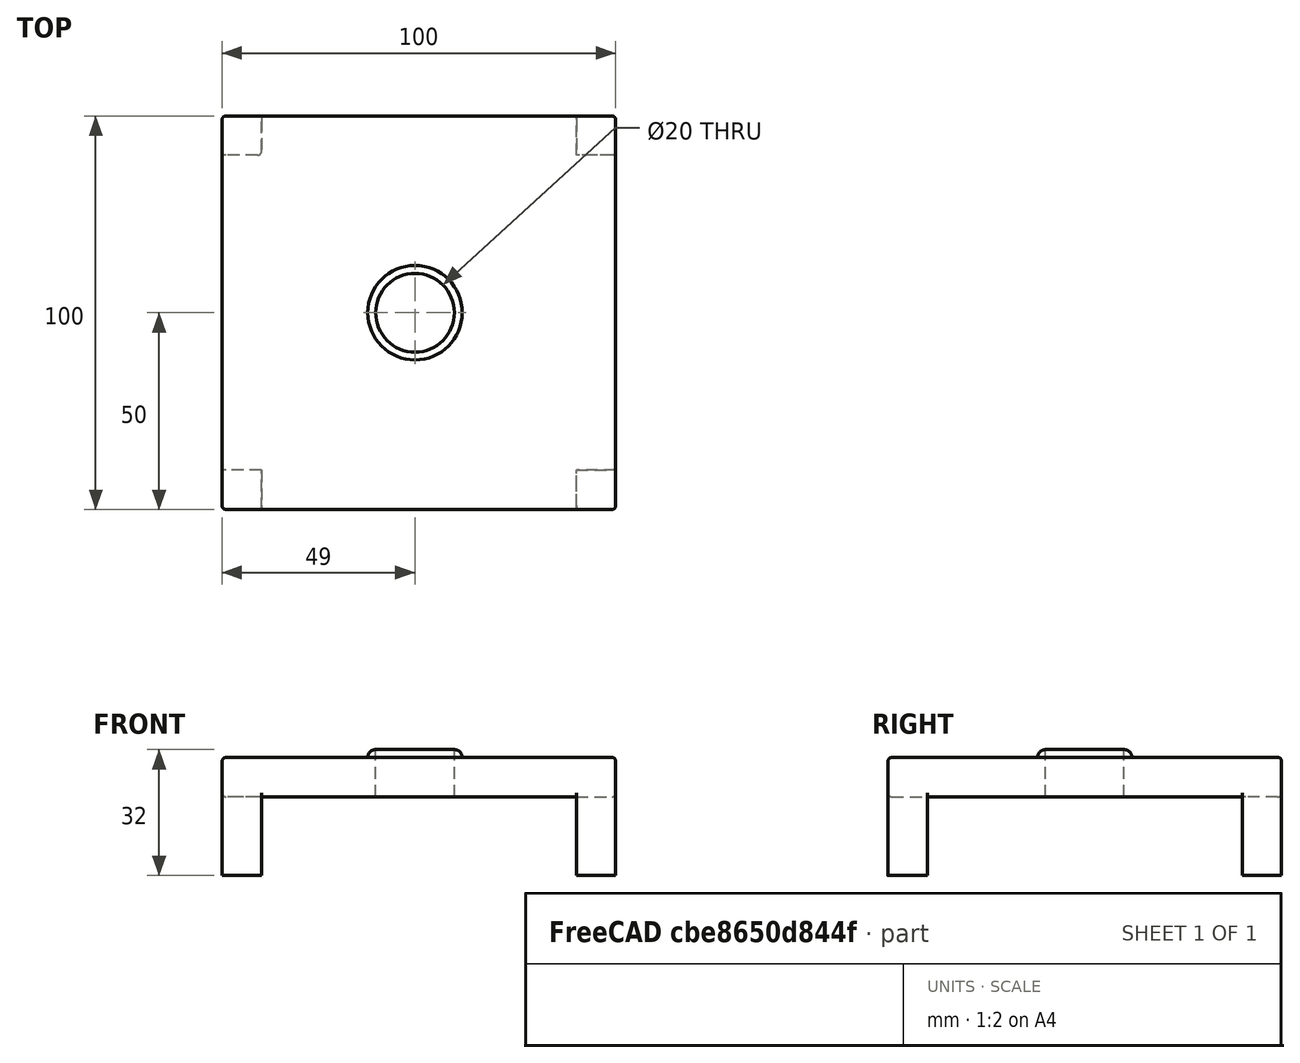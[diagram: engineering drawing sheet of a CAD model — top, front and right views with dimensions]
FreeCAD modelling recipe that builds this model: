
FCSTD DOCUMENT  (FreeCAD 0.18R4 (GitTag))
Label: table
License: All rights reserved
LicenseURL: http://en.wikipedia.org/wiki/All_rights_reserved
objects: Part::Box×5, Part::Fillet×5, Part::Torus×1, Part::FeaturePython×1, Part::Cylinder×1, Part::Cut×1
note: 14 computed .brp shape members not serialized (recipe doc carries the construction recipe); baked Part::Feature solids carry a one-line shape summary decoded from their .brp

FEATURE [Part::Box] Box  label="Cube"
  AttacherType = Attacher::AttachEngine3D
  Height = 10
  Length = 100
  Placement = pos=(-51,-50,0) rot=(0,0,1;0rad)
  Width = 100
FEATURE [Part::Fillet] Fillet
  Base = -> Box
  Edges = 12 edges r=1: [Edge1,Edge2,Edge3,Edge4,Edge5,Edge6,Edge7,Edge8,Edge9,Edge10,Edge11,Edge12]
FEATURE [Part::Box] Box001  label="Cube001"
  AttacherType = Attacher::AttachEngine3D
  Height = 30
  Length = 10
  Placement = pos=(-51,-50,0) rot=(0,0,1;0rad)
  Width = 10
FEATURE [Part::Fillet] Fillet001
  Base = -> Box001
  Edges = 3 edges r=1: [Edge1,Edge4,Edge9]
FEATURE [Part::Box] Box002  label="Cube002"
  AttacherType = Attacher::AttachEngine3D
  Height = 30
  Length = 10
  Placement = pos=(39,40,0) rot=(0,0,1;0rad)
  Width = 10
FEATURE [Part::Fillet] Fillet002
  Base = -> Box002
  Edges = 4 edges r=1: [Edge1,Edge7,Edge8,Edge11]
FEATURE [Part::Box] Box003  label="Cube003"
  AttacherType = Attacher::AttachEngine3D
  Height = 30
  Length = 10
  Placement = pos=(39,-50,0) rot=(0,0,1;0rad)
  Width = 10
FEATURE [Part::Fillet] Fillet003
  Base = -> Box003
  Edges = 3 edges r=1: [Edge4,Edge5,Edge9]
FEATURE [Part::Box] Box004  label="Cube004"
  AttacherType = Attacher::AttachEngine3D
  Height = 30
  Length = 10
  Placement = pos=(-51,40,0) rot=(0,0,1;0rad)
  Width = 10
FEATURE [Part::Fillet] Fillet004
  Base = -> Box004
  Edges = 3 edges r=1: [Edge3,Edge4,Edge11]
FEATURE [Part::Torus] Torus
  Angle1 = -180
  Angle2 = 180
  Angle3 = 360
  AttacherType = Attacher::AttachEngine3D
  Radius1 = 10
  Radius2 = 2
FEATURE [Part::FeaturePython] Connect  # WARN: FeaturePython — macro-defined, semantics opaque (R4)
  Objects = -> [Torus,Fillet003,Fillet002,Fillet004,Fillet,Fillet001]
  Placement = pos=(0,0,0) rot=(0,1,0;3.14159rad)
  Tolerance = 0
FEATURE [Part::Cylinder] Cylinder
  Angle = 360
  AttacherType = Attacher::AttachEngine3D
  Height = 100
  Placement = pos=(0,0,-12) rot=(0,0,1;0rad)
  Radius = 10
FEATURE [Part::Cut] Cut
  Base = -> Connect
  Tool = -> Cylinder
